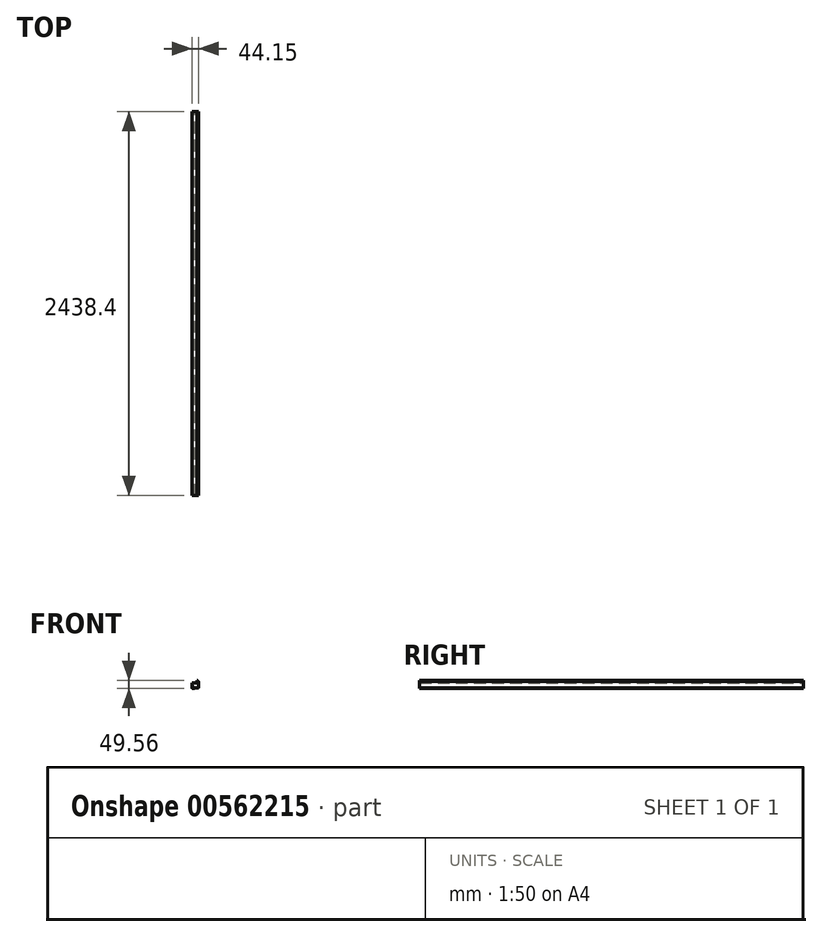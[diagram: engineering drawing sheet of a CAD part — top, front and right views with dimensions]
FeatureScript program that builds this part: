
annotation { "Feature Type Name" : "Feature", "Feature Type Description" : "" }
export const myFeature = defineFeature(function(context is Context, id is Id, definition is map)
    precondition{}
    {
        {
            var Q0;
            Q0=qCreatedBy(makeId("Front.planeOp"),FACE);
            var sketch = newSketch(context, id + "F0", { "sketchPlane" : qUnion([Q0])});
            skLineSegment(sketch, "E0.left", {"start": v(0, 6.12) * mm, "end": v(0, 43.84) * mm});
            skLineSegment(sketch, "E0.right", {"start": v(-44.15, 3.17) * mm, "end": v(-44.15, 33.49) * mm});
            skLineSegment(sketch, "E1.0", {"start": v(-3.17, 2.95) * mm, "end": v(-25.35, 2.95) * mm});
            skLineSegment(sketch, "E2.0", {"start": v(0, 43.84) * mm, "end": v(-2.41, 43.84) * mm});
            skLineSegment(sketch, "E3.0", {"start": v(-11.38, 33.49) * mm, "end": v(-11.38, 49.56) * mm});
            skArc(sketch, "E4", {"start": v(-2.41, 43.84) * mm, "mid": v(-6.21, 47.77) * mm, "end": v(-11.38, 49.56) * mm});
            skPoint(sketch, "E5.orphan", {"position": v(0, 49.56) * mm});
            skLineSegment(sketch, "E6.0", {"start": v(-25.35, 1.61) * mm, "end": v(-25.35, 2.95) * mm});
            skLineSegment(sketch, "E7.trimOffspring", {"start": v(-26.96, 0) * mm, "end": v(-30.77, 0) * mm});
            skLineSegment(sketch, "E8.0", {"start": v(-32.65, 0) * mm, "end": v(-32.65, 7.62) * mm});
            skLineSegment(sketch, "E9.0", {"start": v(-30.77, 0) * mm, "end": v(-30.77, 7.62) * mm});
            skLineSegment(sketch, "E10.0", {"start": v(-30.77, 7.62) * mm, "end": v(-32.65, 7.62) * mm});
            skLineSegment(sketch, "E11.trimOffspring", {"start": v(-32.65, 0) * mm, "end": v(-40.97, 0) * mm});
            skLineSegment(sketch, "E12.trimOffspring", {"start": v(-11.38, 33.49) * mm, "end": v(-44.15, 33.49) * mm});
            skPoint(sketch, "E13.visualSharp", {"position": v(-44.15, 0) * mm});
            skArc(sketch, "E13.filletArc", {"start": v(-44.15, 3.17) * mm, "mid": v(-43.22, 0.93) * mm, "end": v(-40.97, 0) * mm});
            skPoint(sketch, "E14.visualSharp", {"position": v(-25.35, 0) * mm});
            skArc(sketch, "E14.filletArc", {"start": v(-26.96, 0) * mm, "mid": v(-25.82, 0.47) * mm, "end": v(-25.35, 1.61) * mm});
            skArc(sketch, "E15.filletArc", {"start": v(-3.17, 2.95) * mm, "mid": v(-0.93, 3.88) * mm, "end": v(0, 6.12) * mm});
            skSolve(sketch);
        }
        {
            var Q0;
            Q0 = qSketchRegion(id + "F0", true);
            extrude(context, id + "F1", {"entities" : qUnion([Q0]), "depth" : 2438.4 * mm, "offsetDistance" : 25.4 * mm});
        }
    });
